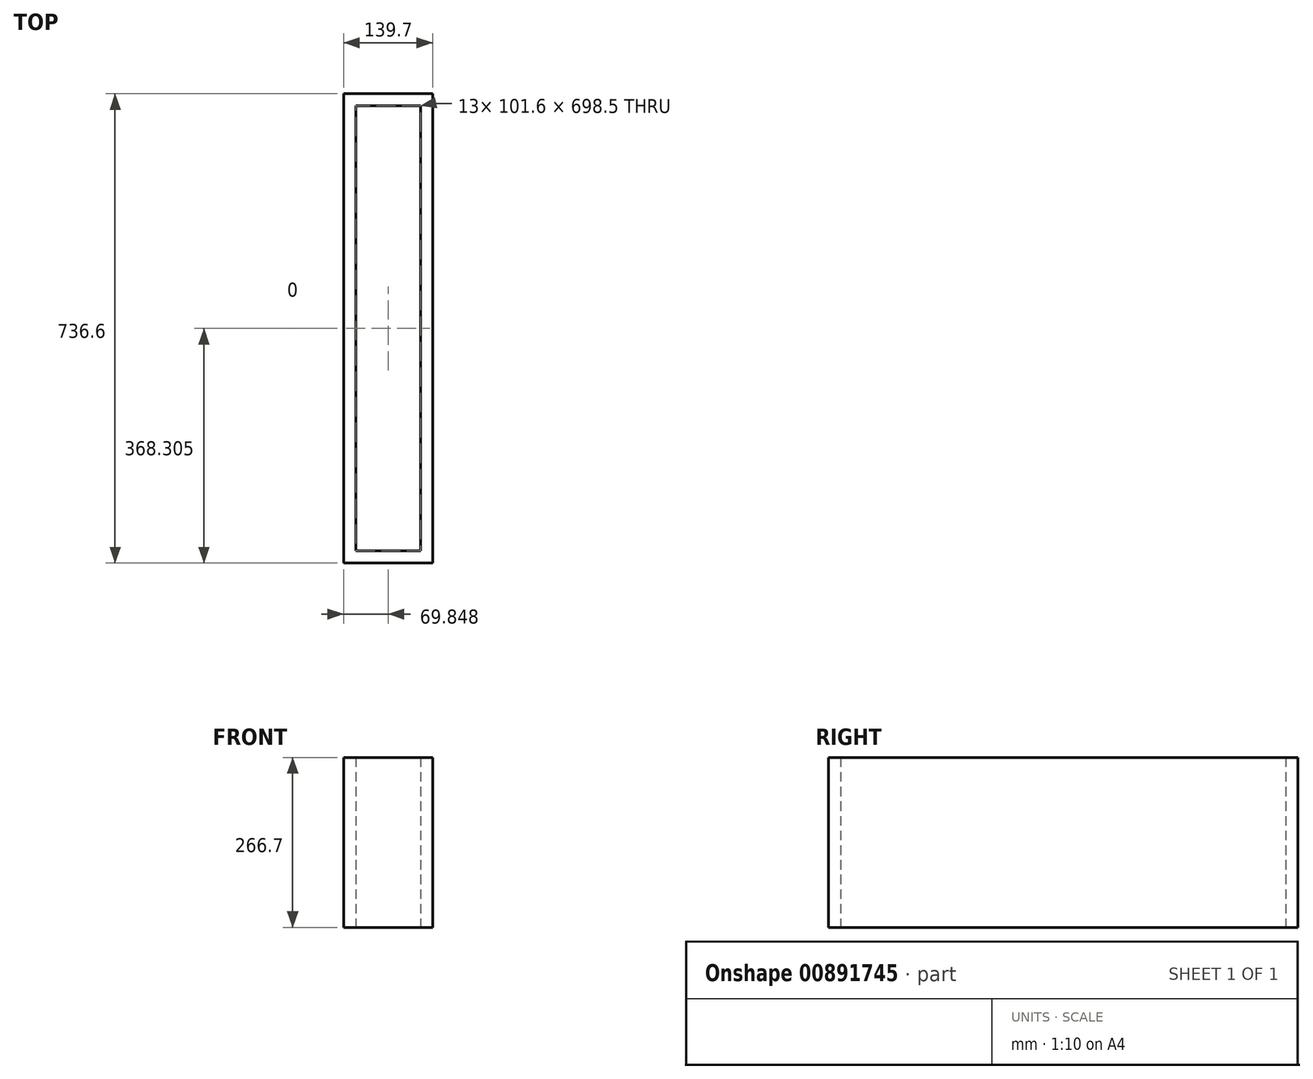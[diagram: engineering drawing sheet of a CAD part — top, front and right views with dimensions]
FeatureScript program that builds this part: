
annotation { "Feature Type Name" : "Feature", "Feature Type Description" : "" }
export const myFeature = defineFeature(function(context is Context, id is Id, definition is map)
    precondition{}
    {
        {
            var Q0;
            Q0=qCreatedBy(makeId("Top.planeOp"),FACE);
            var sketch = newSketch(context, id + "F0", { "sketchPlane" : qUnion([Q0])});
            skLineSegment(sketch, "E0.bottom", {"start": v(-101.8, 577.54) * mm, "end": v(37.9, 577.54) * mm});
            skLineSegment(sketch, "E0.top", {"start": v(-101.8, -159.06) * mm, "end": v(37.9, -159.06) * mm});
            skLineSegment(sketch, "E0.left", {"start": v(-101.8, 577.54) * mm, "end": v(-101.8, -159.06) * mm});
            skLineSegment(sketch, "E0.right", {"start": v(37.9, 577.54) * mm, "end": v(37.9, -159.06) * mm});
            skSolve(sketch);
        }
        {
            var Q0;
            Q0=qSketchRegion(id+"F0",true);
            extrude(context, id + "F1", {"entities" : qUnion([Q0]), "depth" : 266.7 * mm});
        }
        {
            var Q0;
            Q0=makeQuery(id+"F1.opExtrude","CAP_FACE",FACE,{"disambiguationData":[OSD([sQuery(id+"F0.wireOp",EDGE,"E0.bottom"),sQuery(id+"F0.wireOp",EDGE,"E0.top"),sQuery(id+"F0.wireOp",EDGE,"E0.left"),sQuery(id+"F0.wireOp",EDGE,"E0.right")])],"isStart":false});
            var Q1;
            Q1=makeQuery(id+"F1.opExtrude","CAP_FACE",FACE,{"disambiguationData":[OSD([sQuery(id+"F0.wireOp",EDGE,"E0.bottom"),sQuery(id+"F0.wireOp",EDGE,"E0.top"),sQuery(id+"F0.wireOp",EDGE,"E0.left"),sQuery(id+"F0.wireOp",EDGE,"E0.right")])],"isStart":true});
            shell(context, id + "F2", {"entities" : qUnion([Q0, Q1]), "thickness" : 19.05 * mm});
        }
    });
